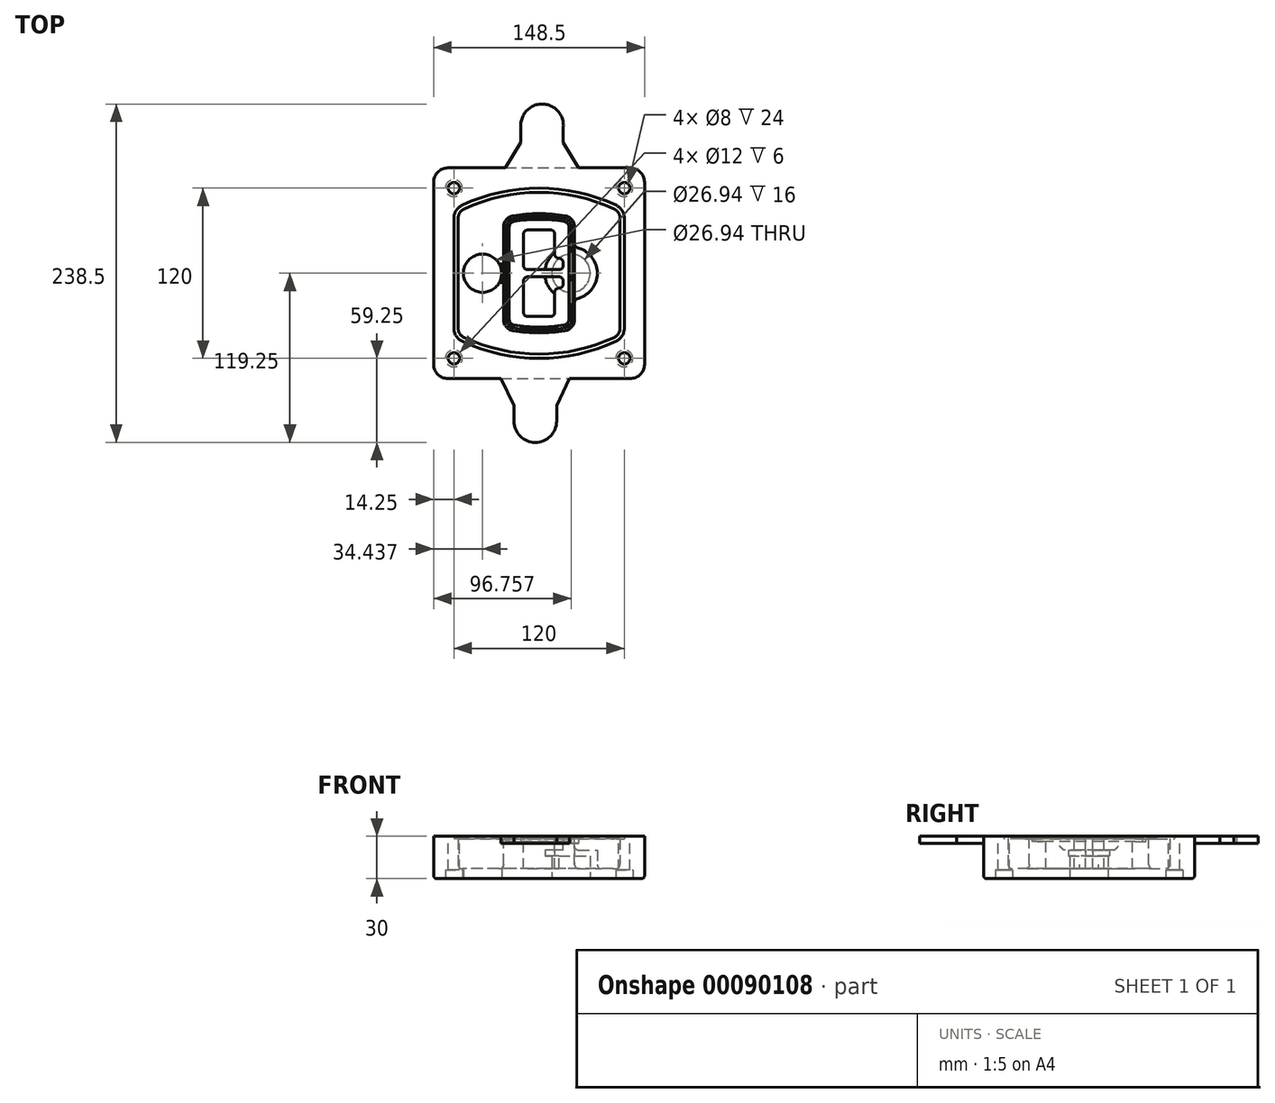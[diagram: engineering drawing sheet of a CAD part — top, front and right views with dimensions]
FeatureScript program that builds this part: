
annotation { "Feature Type Name" : "Feature", "Feature Type Description" : "" }
export const myFeature = defineFeature(function(context is Context, id is Id, definition is map)
    precondition{}
    {
        {
            var Q0;
            Q0=qCreatedBy(makeId("Top.planeOp"),FACE);
            var sketch = newSketch(context, id + "F0", { "sketchPlane" : qUnion([Q0])});
            skPoint(sketch, "E0.rect.middle", {"position": v(0, 0) * mm});
            skLineSegment(sketch, "E1.bottom", {"start": v(-64.25, -74.25) * mm, "end": v(64.25, -74.25) * mm});
            skLineSegment(sketch, "E1.top", {"start": v(-64.25, 74.25) * mm, "end": v(64.25, 74.25) * mm});
            skLineSegment(sketch, "E1.left", {"start": v(-74.25, -64.25) * mm, "end": v(-74.25, 64.25) * mm});
            skLineSegment(sketch, "E1.right", {"start": v(74.25, -64.25) * mm, "end": v(74.25, 64.25) * mm});
            skLineSegment(sketch, "E2", {"start": v(-74.25, 74.25) * mm, "end": v(74.25, -74.25) * mm, "construction": true});
            skLineSegment(sketch, "E3", {"start": v(74.25, 74.25) * mm, "end": v(-74.25, -74.25) * mm, "construction": true});
            skCircle(sketch, "E4", {"center": v(-60, 60) * mm, "radius": 4 * mm});
            skCircle(sketch, "E5", {"center": v(60, 60) * mm, "radius": 4 * mm});
            skCircle(sketch, "E6", {"center": v(60, -60) * mm, "radius": 4 * mm});
            skCircle(sketch, "E7", {"center": v(-60, -60) * mm, "radius": 4 * mm});
            skLineSegment(sketch, "E8", {"start": v(-60, 60) * mm, "end": v(60, 60) * mm, "construction": true});
            skLineSegment(sketch, "E9", {"start": v(60, 60) * mm, "end": v(60, -60) * mm, "construction": true});
            skLineSegment(sketch, "E10", {"start": v(60, -60) * mm, "end": v(-60, -60) * mm, "construction": true});
            skLineSegment(sketch, "E11", {"start": v(-60, -60) * mm, "end": v(-60, 60) * mm, "construction": true});
            skLineSegment(sketch, "E12", {"start": v(-60, 38.83) * mm, "end": v(-60, -38.83) * mm});
            skLineSegment(sketch, "E13", {"start": v(60, 38.83) * mm, "end": v(60, -38.83) * mm});
            skArc(sketch, "E14", {"start": v(54.26, 47.88) * mm, "mid": v(0, 60) * mm, "end": v(-54.26, 47.88) * mm});
            skArc(sketch, "E15", {"start": v(-54.26, -47.88) * mm, "mid": v(0, -60) * mm, "end": v(54.26, -47.88) * mm});
            skLineSegment(sketch, "E16", {"start": v(-60, 0) * mm, "end": v(60, 0) * mm, "construction": true});
            skPoint(sketch, "E17.visualSharp", {"position": v(-60, -45) * mm});
            skArc(sketch, "E17.filletArc", {"start": v(-60, -38.83) * mm, "mid": v(-58.44, -44.2) * mm, "end": v(-54.26, -47.88) * mm});
            skPoint(sketch, "E18.visualSharp", {"position": v(-60, 45) * mm});
            skArc(sketch, "E18.filletArc", {"start": v(-54.26, 47.88) * mm, "mid": v(-58.44, 44.2) * mm, "end": v(-60, 38.83) * mm});
            skPoint(sketch, "E19.visualSharp", {"position": v(60, 45) * mm});
            skArc(sketch, "E19.filletArc", {"start": v(60, 38.83) * mm, "mid": v(58.44, 44.2) * mm, "end": v(54.26, 47.88) * mm});
            skPoint(sketch, "E20.visualSharp", {"position": v(60, -45) * mm});
            skArc(sketch, "E20.filletArc", {"start": v(54.26, -47.88) * mm, "mid": v(58.44, -44.2) * mm, "end": v(60, -38.83) * mm});
            skPoint(sketch, "E21.visualSharp", {"position": v(-74.25, 74.25) * mm});
            skArc(sketch, "E21.filletArc", {"start": v(-64.25, 74.25) * mm, "mid": v(-71.32, 71.32) * mm, "end": v(-74.25, 64.25) * mm});
            skPoint(sketch, "E22.visualSharp", {"position": v(74.25, 74.25) * mm});
            skArc(sketch, "E22.filletArc", {"start": v(74.25, 64.25) * mm, "mid": v(71.32, 71.32) * mm, "end": v(64.25, 74.25) * mm});
            skPoint(sketch, "E23.visualSharp", {"position": v(74.25, -74.25) * mm});
            skArc(sketch, "E23.filletArc", {"start": v(64.25, -74.25) * mm, "mid": v(71.32, -71.32) * mm, "end": v(74.25, -64.25) * mm});
            skPoint(sketch, "E24.visualSharp", {"position": v(-74.25, -74.25) * mm});
            skArc(sketch, "E24.filletArc", {"start": v(-74.25, -64.25) * mm, "mid": v(-71.32, -71.32) * mm, "end": v(-64.25, -74.25) * mm});
            skArc(sketch, "E25.0", {"start": v(57, 38.83) * mm, "mid": v(55.9, 42.58) * mm, "end": v(52.98, 45.17) * mm});
            skLineSegment(sketch, "E25.1", {"start": v(57, 38.83) * mm, "end": v(57, -38.83) * mm});
            skArc(sketch, "E25.2", {"start": v(52.98, -45.17) * mm, "mid": v(55.9, -42.58) * mm, "end": v(57, -38.83) * mm});
            skArc(sketch, "E25.3", {"start": v(-52.98, -45.17) * mm, "mid": v(0, -57) * mm, "end": v(52.98, -45.17) * mm});
            skArc(sketch, "E25.4", {"start": v(-57, -38.83) * mm, "mid": v(-55.9, -42.58) * mm, "end": v(-52.98, -45.17) * mm});
            skArc(sketch, "E25.5", {"start": v(52.98, 45.17) * mm, "mid": v(0, 57) * mm, "end": v(-52.98, 45.17) * mm});
            skLineSegment(sketch, "E25.6", {"start": v(-57, 38.83) * mm, "end": v(-57, -38.83) * mm});
            skArc(sketch, "E25.7", {"start": v(-52.98, 45.17) * mm, "mid": v(-55.9, 42.58) * mm, "end": v(-57, 38.83) * mm});
            skArc(sketch, "E26.0", {"start": v(-55.96, 51.5) * mm, "mid": v(-61.82, 46.33) * mm, "end": v(-64, 38.83) * mm});
            skArc(sketch, "E26.1", {"start": v(55.96, 51.5) * mm, "mid": v(0, 64) * mm, "end": v(-55.96, 51.5) * mm});
            skArc(sketch, "E26.2", {"start": v(64, 38.83) * mm, "mid": v(61.82, 46.33) * mm, "end": v(55.96, 51.5) * mm});
            skLineSegment(sketch, "E26.3", {"start": v(64, 38.83) * mm, "end": v(64, -38.83) * mm});
            skArc(sketch, "E26.4", {"start": v(55.96, -51.5) * mm, "mid": v(61.82, -46.33) * mm, "end": v(64, -38.83) * mm});
            skLineSegment(sketch, "E26.5", {"start": v(-64, 38.83) * mm, "end": v(-64, -38.83) * mm});
            skArc(sketch, "E26.6", {"start": v(-55.96, -51.5) * mm, "mid": v(0, -64) * mm, "end": v(55.96, -51.5) * mm});
            skArc(sketch, "E26.7", {"start": v(-64, -38.83) * mm, "mid": v(-61.82, -46.33) * mm, "end": v(-55.96, -51.5) * mm});
            skSolve(sketch);
        }
        {
            var Q0;
            Q0=makeQuery(id+"F0.imprint","IMPRINT",FACE,{"disambiguationData":[TD([[makeQuery(id+"F0.imprint","IMPRINT",EDGE,{"derivedFrom":sQuery(id+"F0.wireOp",EDGE,"E1.bottom")}),1.0]])]});
            var Q1;
            Q1=makeQuery(id+"F0.imprint","IMPRINT",FACE,{"disambiguationData":[TD([[makeQuery(id+"F0.imprint","IMPRINT",EDGE,{"derivedFrom":sQuery(id+"F0.wireOp",EDGE,"E12")}),1.0]])]});
            var Q2;
            Q2=makeQuery(id+"F0.imprint","IMPRINT",FACE,{"disambiguationData":[TD([[makeQuery(id+"F0.imprint","IMPRINT",EDGE,{"derivedFrom":sQuery(id+"F0.wireOp",EDGE,"E25.0")}),1.0]])]});
            var Q3;
            Q3=makeQuery(id+"F0.imprint","IMPRINT",FACE,{"disambiguationData":[TD([[makeQuery(id+"F0.imprint","IMPRINT",EDGE,{"derivedFrom":sQuery(id+"F0.wireOp",EDGE,"E12")}),-1.0]])]});
            extrude(context, id + "F1", {"entities" : qUnion([Q0, Q1, Q2, Q3]), "oppositeDirection" : true, "depth" : 25 * mm});
        }
        {
            var Q0;
            Q0=makeQuery(id+"F0.imprint","IMPRINT",FACE,{"disambiguationData":[TD([[makeQuery(id+"F0.imprint","IMPRINT",EDGE,{"derivedFrom":sQuery(id+"F0.wireOp",EDGE,"E12")}),1.0]])]});
            extrude(context, id + "F2", {"entities" : qUnion([Q0]), "operationType" : NewBodyOperationType.ADD, "depth" : 3 * mm});
        }
        {
            var Q0;
            Q0=makeQuery(id+"F0.imprint","IMPRINT",FACE,{"disambiguationData":[TD([[makeQuery(id+"F0.imprint","IMPRINT",EDGE,{"derivedFrom":sQuery(id+"F0.wireOp",EDGE,"E25.0")}),1.0]])]});
            extrude(context, id + "F3", {"entities" : qUnion([Q0]), "operationType" : NewBodyOperationType.REMOVE, "oppositeDirection" : true, "depth" : 18 * mm});
        }
        {
            var Q0;
            Q0=makeQuery(id+"F2.opExtrude","CAP_FACE",FACE,{"disambiguationData":[OSD([sQuery(id+"F0.wireOp",EDGE,"E12"),sQuery(id+"F0.wireOp",EDGE,"E13"),sQuery(id+"F0.wireOp",EDGE,"E14"),sQuery(id+"F0.wireOp",EDGE,"E15"),sQuery(id+"F0.wireOp",EDGE,"E17.filletArc"),sQuery(id+"F0.wireOp",EDGE,"E18.filletArc"),sQuery(id+"F0.wireOp",EDGE,"E19.filletArc"),sQuery(id+"F0.wireOp",EDGE,"E20.filletArc"),sQuery(id+"F0.wireOp",EDGE,"E25.0"),sQuery(id+"F0.wireOp",EDGE,"E25.1"),sQuery(id+"F0.wireOp",EDGE,"E25.2"),sQuery(id+"F0.wireOp",EDGE,"E25.3"),sQuery(id+"F0.wireOp",EDGE,"E25.4"),sQuery(id+"F0.wireOp",EDGE,"E25.5"),sQuery(id+"F0.wireOp",EDGE,"E25.6"),sQuery(id+"F0.wireOp",EDGE,"E25.7")])],"isStart":false});
            var sketch = newSketch(context, id + "F4", { "sketchPlane" : qUnion([Q0])});
            skArc(sketch, "E27.0", {"start": v(-18.34, -40.45) * mm, "mid": v(0, -42) * mm, "end": v(18.34, -40.45) * mm});
            skArc(sketch, "E28.0", {"start": v(18.34, 40.45) * mm, "mid": v(0, 42) * mm, "end": v(-18.34, 40.45) * mm});
            skLineSegment(sketch, "E29", {"start": v(-25, 32.57) * mm, "end": v(-25, -32.57) * mm});
            skLineSegment(sketch, "E30", {"start": v(25, 32.57) * mm, "end": v(25, -32.57) * mm});
            skLineSegment(sketch, "E31", {"start": v(-25, 39.1) * mm, "end": v(25, 39.1) * mm, "construction": true});
            skLineSegment(sketch, "E32", {"start": v(-25, -39.1) * mm, "end": v(25, -39.1) * mm, "construction": true});
            skPoint(sketch, "E33.visualSharp", {"position": v(-25, 39.1) * mm});
            skArc(sketch, "E33.filletArc", {"start": v(-18.34, 40.45) * mm, "mid": v(-23.11, 37.73) * mm, "end": v(-25, 32.57) * mm});
            skPoint(sketch, "E34.visualSharp", {"position": v(25, 39.1) * mm});
            skArc(sketch, "E34.filletArc", {"start": v(25, 32.57) * mm, "mid": v(23.11, 37.73) * mm, "end": v(18.34, 40.45) * mm});
            skPoint(sketch, "E35.visualSharp", {"position": v(25, -39.1) * mm});
            skArc(sketch, "E35.filletArc", {"start": v(18.34, -40.45) * mm, "mid": v(23.11, -37.73) * mm, "end": v(25, -32.57) * mm});
            skPoint(sketch, "E36.visualSharp", {"position": v(-25, -39.1) * mm});
            skArc(sketch, "E36.filletArc", {"start": v(-25, -32.57) * mm, "mid": v(-23.11, -37.73) * mm, "end": v(-18.34, -40.45) * mm});
            skArc(sketch, "E37.0", {"start": v(52.98, 45.17) * mm, "mid": v(0, 57) * mm, "end": v(-52.98, 45.17) * mm});
            skArc(sketch, "E37.1", {"start": v(-52.98, 45.17) * mm, "mid": v(-55.9, 42.58) * mm, "end": v(-57, 38.83) * mm});
            skLineSegment(sketch, "E37.2", {"start": v(-57, 38.83) * mm, "end": v(-57, -38.83) * mm});
            skArc(sketch, "E37.3", {"start": v(-57, -38.83) * mm, "mid": v(-55.9, -42.58) * mm, "end": v(-52.98, -45.17) * mm});
            skArc(sketch, "E37.4", {"start": v(-52.98, -45.17) * mm, "mid": v(0, -57) * mm, "end": v(52.98, -45.17) * mm});
            skArc(sketch, "E37.5", {"start": v(52.98, -45.17) * mm, "mid": v(55.9, -42.58) * mm, "end": v(57, -38.83) * mm});
            skLineSegment(sketch, "E37.6", {"start": v(57, 38.83) * mm, "end": v(57, -38.83) * mm});
            skArc(sketch, "E37.7", {"start": v(57, 38.83) * mm, "mid": v(55.9, 42.58) * mm, "end": v(52.98, 45.17) * mm});
            skLineSegment(sketch, "E38.0", {"start": v(23, 32.57) * mm, "end": v(23, -32.57) * mm});
            skArc(sketch, "E38.1", {"start": v(18, -38.48) * mm, "mid": v(21.58, -36.44) * mm, "end": v(23, -32.57) * mm});
            skArc(sketch, "E38.2", {"start": v(-18, -38.48) * mm, "mid": v(0, -40) * mm, "end": v(18, -38.48) * mm});
            skArc(sketch, "E38.3", {"start": v(-23, -32.57) * mm, "mid": v(-21.58, -36.44) * mm, "end": v(-18, -38.48) * mm});
            skLineSegment(sketch, "E38.4", {"start": v(-23, 32.57) * mm, "end": v(-23, -32.57) * mm});
            skArc(sketch, "E38.5", {"start": v(23, 32.57) * mm, "mid": v(21.58, 36.44) * mm, "end": v(18, 38.48) * mm});
            skArc(sketch, "E38.6", {"start": v(-18, 38.48) * mm, "mid": v(-21.58, 36.44) * mm, "end": v(-23, 32.57) * mm});
            skArc(sketch, "E38.7", {"start": v(18, 38.48) * mm, "mid": v(0, 40) * mm, "end": v(-18, 38.48) * mm});
            skArc(sketch, "E39.0", {"start": v(21, 32.57) * mm, "mid": v(20.06, 35.15) * mm, "end": v(17.67, 36.5) * mm});
            skLineSegment(sketch, "E39.1", {"start": v(21, 32.57) * mm, "end": v(21, -32.57) * mm});
            skArc(sketch, "E39.2", {"start": v(17.67, -36.5) * mm, "mid": v(20.06, -35.15) * mm, "end": v(21, -32.57) * mm});
            skArc(sketch, "E39.3", {"start": v(-17.67, -36.5) * mm, "mid": v(0, -38) * mm, "end": v(17.67, -36.5) * mm});
            skArc(sketch, "E39.4", {"start": v(-21, -32.57) * mm, "mid": v(-20.06, -35.15) * mm, "end": v(-17.67, -36.5) * mm});
            skArc(sketch, "E39.5", {"start": v(17.67, 36.5) * mm, "mid": v(0, 38) * mm, "end": v(-17.67, 36.5) * mm});
            skLineSegment(sketch, "E39.6", {"start": v(-21, 32.57) * mm, "end": v(-21, -32.57) * mm});
            skArc(sketch, "E39.7", {"start": v(-17.67, 36.5) * mm, "mid": v(-20.06, 35.15) * mm, "end": v(-21, 32.57) * mm});
            skLineSegment(sketch, "E40", {"start": v(-25, 0) * mm, "end": v(25, 0) * mm, "construction": true});
            skLineSegment(sketch, "E41", {"start": v(-11, 5.5) * mm, "end": v(-11, 27.5) * mm});
            skLineSegment(sketch, "E42", {"start": v(-8, 30.5) * mm, "end": v(8, 30.5) * mm});
            skLineSegment(sketch, "E43", {"start": v(11, 27.5) * mm, "end": v(11, 13.5) * mm});
            skLineSegment(sketch, "E44", {"start": v(14, 10.5) * mm, "end": v(14, 10.5) * mm});
            skLineSegment(sketch, "E45", {"start": v(17, 7.5) * mm, "end": v(17, 5.5) * mm});
            skLineSegment(sketch, "E46", {"start": v(14, 2.5) * mm, "end": v(-8, 2.5) * mm});
            skPoint(sketch, "E47.visualSharp", {"position": v(-11, 30.5) * mm});
            skArc(sketch, "E47.filletArc", {"start": v(-8, 30.5) * mm, "mid": v(-10.12, 29.62) * mm, "end": v(-11, 27.5) * mm});
            skPoint(sketch, "E48.visualSharp", {"position": v(11, 30.5) * mm});
            skArc(sketch, "E48.filletArc", {"start": v(11, 27.5) * mm, "mid": v(10.12, 29.62) * mm, "end": v(8, 30.5) * mm});
            skPoint(sketch, "E49.visualSharp", {"position": v(11, 10.5) * mm});
            skArc(sketch, "E49.filletArc", {"start": v(11, 13.5) * mm, "mid": v(11.88, 11.38) * mm, "end": v(14, 10.5) * mm});
            skPoint(sketch, "E50.visualSharp", {"position": v(17, 10.5) * mm});
            skArc(sketch, "E50.filletArc", {"start": v(17, 7.5) * mm, "mid": v(16.12, 9.62) * mm, "end": v(14, 10.5) * mm});
            skPoint(sketch, "E51.visualSharp", {"position": v(17, 2.5) * mm});
            skArc(sketch, "E51.filletArc", {"start": v(14, 2.5) * mm, "mid": v(16.12, 3.38) * mm, "end": v(17, 5.5) * mm});
            skPoint(sketch, "E52.visualSharp", {"position": v(-11, 2.5) * mm});
            skArc(sketch, "E52.filletArc", {"start": v(-11, 5.5) * mm, "mid": v(-10.12, 3.38) * mm, "end": v(-8, 2.5) * mm});
            skLineSegment(sketch, "E53.0.MirrorCS", {"start": v(14, -2.5) * mm, "end": v(-8, -2.5) * mm});
            skArc(sketch, "E54.0.MirrorCS", {"start": v(-11, -5.5) * mm, "mid": v(-10.12, -3.38) * mm, "end": v(-8, -2.5) * mm});
            skLineSegment(sketch, "E55.0.MirrorCS", {"start": v(-11, -5.5) * mm, "end": v(-11, -27.5) * mm});
            skArc(sketch, "E56.0.MirrorCS", {"start": v(-8, -30.5) * mm, "mid": v(-10.12, -29.62) * mm, "end": v(-11, -27.5) * mm});
            skLineSegment(sketch, "E57.0.MirrorCS", {"start": v(-8, -30.5) * mm, "end": v(8, -30.5) * mm});
            skArc(sketch, "E58.0.MirrorCS", {"start": v(11, -27.5) * mm, "mid": v(10.12, -29.62) * mm, "end": v(8, -30.5) * mm});
            skLineSegment(sketch, "E59.0.MirrorCS", {"start": v(11, -27.5) * mm, "end": v(11, -13.5) * mm});
            skArc(sketch, "E60.0.MirrorCS", {"start": v(11, -13.5) * mm, "mid": v(11.88, -11.38) * mm, "end": v(14, -10.5) * mm});
            skArc(sketch, "E61.0.MirrorCS", {"start": v(17, -7.5) * mm, "mid": v(16.12, -9.62) * mm, "end": v(14, -10.5) * mm});
            skLineSegment(sketch, "E62.0.MirrorCS", {"start": v(17, -7.5) * mm, "end": v(17, -5.5) * mm});
            skArc(sketch, "E63.0.MirrorCS", {"start": v(14, -2.5) * mm, "mid": v(16.12, -3.38) * mm, "end": v(17, -5.5) * mm});
            skSolve(sketch);
        }
        {
            var Q0;
            Q0=makeQuery(id+"F4.imprint","IMPRINT",FACE,{"disambiguationData":[TD([[makeQuery(id+"F4.imprint","IMPRINT",EDGE,{"derivedFrom":sQuery(id+"F4.wireOp",EDGE,"E27.0")}),1.0]])]});
            var Q1;
            Q1=makeQuery(id+"F4.imprint","IMPRINT",FACE,{"disambiguationData":[TD([[makeQuery(id+"F4.imprint","IMPRINT",EDGE,{"derivedFrom":sQuery(id+"F4.wireOp",EDGE,"E38.0")}),-1.0]])]});
            var Q2;
            Q2=makeQuery(id+"F4.imprint","IMPRINT",FACE,{"disambiguationData":[TD([[makeQuery(id+"F4.imprint","IMPRINT",EDGE,{"derivedFrom":sQuery(id+"F4.wireOp",EDGE,"E39.0")}),1.0]])]});
            extrude(context, id + "F5", {"entities" : qUnion([Q0, Q1, Q2]), "operationType" : NewBodyOperationType.ADD, "endBound" : BoundingType.UP_TO_NEXT, "oppositeDirection" : true, "depth" : 25 * mm});
        }
        {
            var Q0;
            Q0=makeQuery(id+"F4.imprint","IMPRINT",FACE,{"disambiguationData":[TD([[makeQuery(id+"F4.imprint","IMPRINT",EDGE,{"derivedFrom":sQuery(id+"F4.wireOp",EDGE,"E38.0")}),-1.0]])]});
            extrude(context, id + "F6", {"entities" : qUnion([Q0]), "operationType" : NewBodyOperationType.REMOVE, "oppositeDirection" : true, "depth" : 2 * mm});
        }
        {
            var Q0;
            Q0=makeQuery(id+"F1.opExtrude","CAP_FACE",FACE,{"disambiguationData":[OSD([sQuery(id+"F0.wireOp",EDGE,"E1.bottom"),sQuery(id+"F0.wireOp",EDGE,"E1.top"),sQuery(id+"F0.wireOp",EDGE,"E1.left"),sQuery(id+"F0.wireOp",EDGE,"E1.right"),sQuery(id+"F0.wireOp",EDGE,"E4"),sQuery(id+"F0.wireOp",EDGE,"E5"),sQuery(id+"F0.wireOp",EDGE,"E6"),sQuery(id+"F0.wireOp",EDGE,"E7"),sQuery(id+"F0.wireOp",EDGE,"E21.filletArc"),sQuery(id+"F0.wireOp",EDGE,"E22.filletArc"),sQuery(id+"F0.wireOp",EDGE,"E23.filletArc"),sQuery(id+"F0.wireOp",EDGE,"E24.filletArc")])],"isStart":false});
            var sketch = newSketch(context, id + "F7", { "sketchPlane" : qUnion([Q0])});
            skCircle(sketch, "E64", {"center": v(22.5, 0) * mm, "radius": 13.47 * mm});
            skCircle(sketch, "E65", {"center": v(-39.81, 0) * mm, "radius": 13.47 * mm});
            skLineSegment(sketch, "E66", {"start": v(74.25, 0) * mm, "end": v(-74.25, 0) * mm});
            skCircle(sketch, "E67", {"center": v(22.5, 0) * mm, "radius": 18.47 * mm});
            skCircle(sketch, "E68", {"center": v(60, -60) * mm, "radius": 6 * mm});
            skCircle(sketch, "E69", {"center": v(-60, -60) * mm, "radius": 6 * mm});
            skCircle(sketch, "E70", {"center": v(-60, 60) * mm, "radius": 6 * mm});
            skCircle(sketch, "E71", {"center": v(60, 60) * mm, "radius": 6 * mm});
            skSolve(sketch);
        }
        {
            var Q0;
            {var subQ1=sQuery(id+"F7.wireOp",EDGE,"E66");var subQ4=sQuery(id+"F7.wireOp",EDGE,"E64");var subQ6=makeQuery(id+"F7.imprint","INTERSECT",VERTEX,{"disambiguationData":[OD(0.0)],"derivedFrom":[subQ4,subQ1]});Q0=makeQuery(id+"F7.imprint","IMPRINT",FACE,{"disambiguationData":[TD([[makeQuery(id+"F7.imprint","IMPRINT",EDGE,{"disambiguationData":[TD([[subQ6,-1.0]])],"derivedFrom":subQ4}),-1.0]])]});}
            var Q1;
            {var subQ0=sQuery(id+"F7.wireOp",EDGE,"E66");var subQ1=sQuery(id+"F7.wireOp",EDGE,"E64");var subQ3=makeQuery(id+"F7.imprint","INTERSECT",VERTEX,{"disambiguationData":[OD(0.0)],"derivedFrom":[subQ1,subQ0]});Q1=makeQuery(id+"F7.imprint","IMPRINT",FACE,{"disambiguationData":[TD([[makeQuery(id+"F7.imprint","IMPRINT",EDGE,{"disambiguationData":[TD([[subQ3,-1.0]])],"derivedFrom":subQ1}),1.0]])]});}
            var Q2;
            {var subQ0=sQuery(id+"F7.wireOp",EDGE,"E66");var subQ1=sQuery(id+"F7.wireOp",EDGE,"E64");var subQ3=makeQuery(id+"F7.imprint","INTERSECT",VERTEX,{"disambiguationData":[OD(0.0)],"derivedFrom":[subQ1,subQ0]});Q2=makeQuery(id+"F7.imprint","IMPRINT",FACE,{"disambiguationData":[TD([[makeQuery(id+"F7.imprint","IMPRINT",EDGE,{"disambiguationData":[TD([[subQ3,1.0]])],"derivedFrom":subQ1}),1.0]])]});}
            var Q3;
            {var subQ1=sQuery(id+"F7.wireOp",EDGE,"E66");var subQ4=sQuery(id+"F7.wireOp",EDGE,"E64");var subQ6=makeQuery(id+"F7.imprint","INTERSECT",VERTEX,{"disambiguationData":[OD(0.0)],"derivedFrom":[subQ4,subQ1]});Q3=makeQuery(id+"F7.imprint","IMPRINT",FACE,{"disambiguationData":[TD([[makeQuery(id+"F7.imprint","IMPRINT",EDGE,{"disambiguationData":[TD([[subQ6,1.0]])],"derivedFrom":subQ4}),-1.0]])]});}
            extrude(context, id + "F8", {"entities" : qUnion([Q0, Q1, Q2, Q3]), "operationType" : NewBodyOperationType.ADD, "oppositeDirection" : true, "depth" : 20 * mm});
        }
        {
            var Q0;
            {var subQ0=sQuery(id+"F7.wireOp",EDGE,"E66");var subQ1=sQuery(id+"F7.wireOp",EDGE,"E64");var subQ3=makeQuery(id+"F7.imprint","INTERSECT",VERTEX,{"disambiguationData":[OD(0.0)],"derivedFrom":[subQ1,subQ0]});Q0=makeQuery(id+"F7.imprint","IMPRINT",FACE,{"disambiguationData":[TD([[makeQuery(id+"F7.imprint","IMPRINT",EDGE,{"disambiguationData":[TD([[subQ3,-1.0]])],"derivedFrom":subQ1}),1.0]])]});}
            var Q1;
            {var subQ0=sQuery(id+"F7.wireOp",EDGE,"E66");var subQ1=sQuery(id+"F7.wireOp",EDGE,"E64");var subQ3=makeQuery(id+"F7.imprint","INTERSECT",VERTEX,{"disambiguationData":[OD(0.0)],"derivedFrom":[subQ1,subQ0]});Q1=makeQuery(id+"F7.imprint","IMPRINT",FACE,{"disambiguationData":[TD([[makeQuery(id+"F7.imprint","IMPRINT",EDGE,{"disambiguationData":[TD([[subQ3,1.0]])],"derivedFrom":subQ1}),1.0]])]});}
            extrude(context, id + "F9", {"entities" : qUnion([Q0, Q1]), "operationType" : NewBodyOperationType.REMOVE, "oppositeDirection" : true, "depth" : 16 * mm});
        }
        {
            var Q0;
            {var subQ0=sQuery(id+"F7.wireOp",EDGE,"E66");var subQ1=sQuery(id+"F7.wireOp",EDGE,"E65");var subQ3=makeQuery(id+"F7.imprint","INTERSECT",VERTEX,{"disambiguationData":[OD(0.0)],"derivedFrom":[subQ1,subQ0]});Q0=makeQuery(id+"F7.imprint","IMPRINT",FACE,{"disambiguationData":[TD([[makeQuery(id+"F7.imprint","IMPRINT",EDGE,{"disambiguationData":[TD([[subQ3,-1.0]])],"derivedFrom":subQ1}),1.0]])]});}
            var Q1;
            {var subQ0=sQuery(id+"F7.wireOp",EDGE,"E66");var subQ1=sQuery(id+"F7.wireOp",EDGE,"E65");var subQ3=makeQuery(id+"F7.imprint","INTERSECT",VERTEX,{"disambiguationData":[OD(0.0)],"derivedFrom":[subQ1,subQ0]});Q1=makeQuery(id+"F7.imprint","IMPRINT",FACE,{"disambiguationData":[TD([[makeQuery(id+"F7.imprint","IMPRINT",EDGE,{"disambiguationData":[TD([[subQ3,1.0]])],"derivedFrom":subQ1}),1.0]])]});}
            extrude(context, id + "F10", {"entities" : qUnion([Q0, Q1]), "operationType" : NewBodyOperationType.REMOVE, "oppositeDirection" : true, "depth" : 25 * mm});
        }
        {
            var Q0;
            Q0=makeQuery(id+"F7.imprint","IMPRINT",FACE,{"disambiguationData":[TD([[makeQuery(id+"F7.imprint","IMPRINT",EDGE,{"derivedFrom":sQuery(id+"F7.wireOp",EDGE,"E68")}),1.0]])]});
            var Q1;
            Q1=makeQuery(id+"F7.imprint","IMPRINT",FACE,{"disambiguationData":[TD([[makeQuery(id+"F7.imprint","IMPRINT",EDGE,{"derivedFrom":makeQuery(id+"F1.opExtrude","CAP_EDGE",EDGE,{"disambiguationData":[OSD([sQuery(id+"F0.wireOp",EDGE,"E5")])],"isStart":false})}),-1.0]])]});
            var Q2;
            Q2=makeQuery(id+"F7.imprint","IMPRINT",FACE,{"disambiguationData":[TD([[makeQuery(id+"F7.imprint","IMPRINT",EDGE,{"derivedFrom":sQuery(id+"F7.wireOp",EDGE,"E69")}),1.0]])]});
            var Q3;
            Q3=makeQuery(id+"F7.imprint","IMPRINT",FACE,{"disambiguationData":[TD([[makeQuery(id+"F7.imprint","IMPRINT",EDGE,{"derivedFrom":makeQuery(id+"F1.opExtrude","CAP_EDGE",EDGE,{"disambiguationData":[OSD([sQuery(id+"F0.wireOp",EDGE,"E4")])],"isStart":false})}),-1.0]])]});
            var Q4;
            Q4=makeQuery(id+"F7.imprint","IMPRINT",FACE,{"disambiguationData":[TD([[makeQuery(id+"F7.imprint","IMPRINT",EDGE,{"derivedFrom":sQuery(id+"F7.wireOp",EDGE,"E70")}),1.0]])]});
            var Q5;
            Q5=makeQuery(id+"F7.imprint","IMPRINT",FACE,{"disambiguationData":[TD([[makeQuery(id+"F7.imprint","IMPRINT",EDGE,{"derivedFrom":makeQuery(id+"F1.opExtrude","CAP_EDGE",EDGE,{"disambiguationData":[OSD([sQuery(id+"F0.wireOp",EDGE,"E7")])],"isStart":false})}),-1.0]])]});
            var Q6;
            Q6=makeQuery(id+"F7.imprint","IMPRINT",FACE,{"disambiguationData":[TD([[makeQuery(id+"F7.imprint","IMPRINT",EDGE,{"derivedFrom":sQuery(id+"F7.wireOp",EDGE,"E71")}),1.0]])]});
            var Q7;
            Q7=makeQuery(id+"F7.imprint","IMPRINT",FACE,{"disambiguationData":[TD([[makeQuery(id+"F7.imprint","IMPRINT",EDGE,{"derivedFrom":makeQuery(id+"F1.opExtrude","CAP_EDGE",EDGE,{"disambiguationData":[OSD([sQuery(id+"F0.wireOp",EDGE,"E6")])],"isStart":false})}),-1.0]])]});
            extrude(context, id + "F11", {"entities" : qUnion([Q0, Q1, Q2, Q3, Q4, Q5, Q6, Q7]), "operationType" : NewBodyOperationType.REMOVE, "oppositeDirection" : true, "depth" : 6 * mm});
        }
        {
            var Q0;
            Q0=makeQuery(id+"F9.boolean.opBoolean","COPY",FACE,{"derivedFrom":makeQuery(id+"F9.opExtrude","CAP_FACE",FACE,{"disambiguationData":[OSD([sQuery(id+"F7.wireOp",EDGE,"E64")])],"isStart":false})});
            var sketch = newSketch(context, id + "F12", { "sketchPlane" : qUnion([Q0])});
            skArc(sketch, "E72.0", {"start": v(11, 14.45) * mm, "mid": v(6.45, 9.13) * mm, "end": v(4.2, 2.5) * mm});
            skArc(sketch, "E72.1", {"start": v(4.2, -2.5) * mm, "mid": v(6.45, -9.13) * mm, "end": v(11, -14.45) * mm});
            skLineSegment(sketch, "E73", {"start": v(4.2, -2.5) * mm, "end": v(14, -2.5) * mm});
            skLineSegment(sketch, "E74.0", {"start": v(14, 2.5) * mm, "end": v(4.2, 2.5) * mm});
            skArc(sketch, "E74.1", {"start": v(14, 2.5) * mm, "mid": v(16.12, 3.38) * mm, "end": v(17, 5.5) * mm});
            skLineSegment(sketch, "E74.2", {"start": v(17, 7.5) * mm, "end": v(17, 5.5) * mm});
            skArc(sketch, "E74.3", {"start": v(17, 7.5) * mm, "mid": v(16.12, 9.62) * mm, "end": v(14, 10.5) * mm});
            skArc(sketch, "E74.4", {"start": v(11, 13.5) * mm, "mid": v(11.88, 11.38) * mm, "end": v(14, 10.5) * mm});
            skLineSegment(sketch, "E74.5", {"start": v(11, 14.45) * mm, "end": v(11, 13.5) * mm});
            skLineSegment(sketch, "E74.7", {"start": v(14, -2.5) * mm, "end": v(4.2, -2.5) * mm});
            skArc(sketch, "E74.8", {"start": v(14, -2.5) * mm, "mid": v(16.12, -3.38) * mm, "end": v(17, -5.5) * mm});
            skLineSegment(sketch, "E74.9", {"start": v(17, -7.5) * mm, "end": v(17, -5.5) * mm});
            skArc(sketch, "E74.10", {"start": v(17, -7.5) * mm, "mid": v(16.12, -9.62) * mm, "end": v(14, -10.5) * mm});
            skArc(sketch, "E74.11", {"start": v(11, -13.5) * mm, "mid": v(11.88, -11.38) * mm, "end": v(14, -10.5) * mm});
            skLineSegment(sketch, "E74.12", {"start": v(11, -14.45) * mm, "end": v(11, -13.5) * mm});
            skPoint(sketch, "E75.orphan", {"position": v(11, -27.5) * mm});
            skPoint(sketch, "E76.orphan", {"position": v(-8, -2.5) * mm});
            skPoint(sketch, "E77.orphan", {"position": v(-8, 2.5) * mm});
            skPoint(sketch, "E78.orphan", {"position": v(11, 27.5) * mm});
            skSolve(sketch);
        }
        {
            var Q0;
            {var subQ7=sQuery(id+"F12.wireOp",EDGE,"E72.0");var subQ14=sQuery(id+"F12.wireOp",EDGE,"E72.1");var subQ16=sQuery(id+"F12.wireOp",EDGE,"E74.1");var subQ18=sQuery(id+"F12.wireOp",EDGE,"E74.8");Q0=qUnion([makeQuery(id+"F12.imprint","IMPRINT",FACE,{"disambiguationData":[TD([[makeQuery(id+"F12.imprint","IMPRINT",EDGE,{"derivedFrom":subQ7}),1.0]])]}),makeQuery(id+"F12.imprint","IMPRINT",FACE,{"disambiguationData":[TD([[makeQuery(id+"F12.imprint","IMPRINT",EDGE,{"derivedFrom":subQ14}),1.0]])]}),makeQuery(id+"F12.imprint","IMPRINT",FACE,{"disambiguationData":[TD([[makeQuery(id+"F12.imprint","IMPRINT",EDGE,{"derivedFrom":subQ16}),1.0]])]}),makeQuery(id+"F12.imprint","IMPRINT",FACE,{"disambiguationData":[TD([[makeQuery(id+"F12.imprint","IMPRINT",EDGE,{"derivedFrom":subQ18}),-1.0]])]})]);}
            var Q1;
            Q1=makeQuery(id+"F5.boolean.opBoolean","SPLIT",FACE,{"disambiguationData":[TD([makeQuery(id+"F5.opExtrude","SWEPT_FACE",FACE,{"disambiguationData":[OSD([sQuery(id+"F4.wireOp",EDGE,"E41")])]})])],"derivedFrom":makeQuery(id+"F3.boolean.opBoolean","COPY",FACE,{"derivedFrom":makeQuery(id+"F3.opExtrude","CAP_FACE",FACE,{"disambiguationData":[OSD([sQuery(id+"F0.wireOp",EDGE,"E25.0"),sQuery(id+"F0.wireOp",EDGE,"E25.1"),sQuery(id+"F0.wireOp",EDGE,"E25.2"),sQuery(id+"F0.wireOp",EDGE,"E25.3"),sQuery(id+"F0.wireOp",EDGE,"E25.4"),sQuery(id+"F0.wireOp",EDGE,"E25.5"),sQuery(id+"F0.wireOp",EDGE,"E25.6"),sQuery(id+"F0.wireOp",EDGE,"E25.7")])],"isStart":false})})});
            extrude(context, id + "F13", {"entities" : qUnion([Q0]), "operationType" : NewBodyOperationType.REMOVE, "endBound" : BoundingType.UP_TO_SURFACE, "endBoundEntityFace" : qUnion([Q1]), "depth" : 25 * mm});
        }
        {
            var Q0;
            Q0=makeQuery(id+"F3.boolean.opBoolean","COPY",EDGE,{"derivedFrom":makeQuery(id+"F3.opExtrude","CAP_EDGE",EDGE,{"disambiguationData":[OSD([sQuery(id+"F0.wireOp",EDGE,"E25.6")])],"isStart":false})});
            var Q1;
            Q1=makeQuery(id+"F8.boolean.opBoolean","INTERSECT",EDGE,{"derivedFrom":[makeQuery(id+"F5.opExtrude","SWEPT_FACE",FACE,{"disambiguationData":[OSD([sQuery(id+"F4.wireOp",EDGE,"E30")])]}),makeQuery(id+"F8.opExtrude","CAP_FACE",FACE,{"disambiguationData":[OSD([sQuery(id+"F7.wireOp",EDGE,"E67")])],"isStart":false})]});
            var Q2;
            Q2=makeQuery(id+"F8.boolean.opBoolean","INTERSECT",EDGE,{"disambiguationData":[OD(1.0)],"derivedFrom":[makeQuery(id+"F5.opExtrude","SWEPT_FACE",FACE,{"disambiguationData":[OSD([sQuery(id+"F4.wireOp",EDGE,"E30")])]}),makeQuery(id+"F8.opExtrude","SWEPT_FACE",FACE,{"disambiguationData":[OSD([sQuery(id+"F7.wireOp",EDGE,"E67")])]})]});
            var Q3;
            {var subQ0=sQuery(id+"F4.wireOp",EDGE,"E30");Q3=makeQuery(id+"F8.boolean.opBoolean","SPLIT",EDGE,{"disambiguationData":[TD([makeQuery(id+"F5.opExtrude","SWEPT_FACE",FACE,{"disambiguationData":[OSD([sQuery(id+"F4.wireOp",EDGE,"E35.filletArc")])]})])],"derivedFrom":makeQuery(id+"F5.opExtrude","CAP_EDGE",EDGE,{"disambiguationData":[OSD([subQ0])],"isStart":false})});}
            var Q4;
            {var subQ0=sQuery(id+"F0.wireOp",EDGE,"E25.7");var subQ1=sQuery(id+"F0.wireOp",EDGE,"E25.1");var subQ2=sQuery(id+"F0.wireOp",EDGE,"E25.6");var subQ3=sQuery(id+"F0.wireOp",EDGE,"E25.5");var subQ4=sQuery(id+"F0.wireOp",EDGE,"E25.4");var subQ5=sQuery(id+"F0.wireOp",EDGE,"E25.0");var subQ6=sQuery(id+"F0.wireOp",EDGE,"E25.2");var subQ7=sQuery(id+"F0.wireOp",EDGE,"E25.3");Q4=makeQuery(id+"F8.boolean.opBoolean","INTERSECT",EDGE,{"derivedFrom":[makeQuery(id+"F5.boolean.opBoolean","SPLIT",FACE,{"disambiguationData":[TD([makeQuery(id+"F2.opExtrude","SWEPT_FACE",FACE,{"disambiguationData":[OSD([subQ5])]})])],"derivedFrom":makeQuery(id+"F3.boolean.opBoolean","COPY",FACE,{"derivedFrom":makeQuery(id+"F3.opExtrude","CAP_FACE",FACE,{"disambiguationData":[OSD([subQ5,subQ1,subQ6,subQ7,subQ4,subQ3,subQ2,subQ0])],"isStart":false})})}),makeQuery(id+"F8.opExtrude","SWEPT_FACE",FACE,{"disambiguationData":[OSD([sQuery(id+"F7.wireOp",EDGE,"E67")])]})]});}
            var Q5;
            Q5=makeQuery(id+"F8.boolean.opBoolean","INTERSECT",EDGE,{"disambiguationData":[OD(0.0)],"derivedFrom":[makeQuery(id+"F5.opExtrude","SWEPT_FACE",FACE,{"disambiguationData":[OSD([sQuery(id+"F4.wireOp",EDGE,"E30")])]}),makeQuery(id+"F8.opExtrude","SWEPT_FACE",FACE,{"disambiguationData":[OSD([sQuery(id+"F7.wireOp",EDGE,"E67")])]})]});
            fillet(context, id + "F14", {"entities" : qUnion([Q0, Q1, Q2, Q3, Q4, Q5]), "radius" : 3 * mm, "tangentPropagation" : true, "allowEdgeOverflow" : false});
        }
        {
            var Q0;
            Q0=makeQuery(id+"F1.opExtrude","CAP_EDGE",EDGE,{"disambiguationData":[OSD([sQuery(id+"F0.wireOp",EDGE,"E1.bottom")])],"isStart":false});
            fillet(context, id + "F15", {"entities" : qUnion([Q0]), "radius" : 2 * mm, "tangentPropagation" : true, "allowEdgeOverflow" : false});
        }
        {
            var Q0;
            {var subQ0=sQuery(id+"F0.wireOp",EDGE,"E22.filletArc");var subQ1=sQuery(id+"F0.wireOp",EDGE,"E7");var subQ2=sQuery(id+"F0.wireOp",EDGE,"E6");var subQ3=sQuery(id+"F0.wireOp",EDGE,"E5");var subQ4=sQuery(id+"F0.wireOp",EDGE,"E4");var subQ5=sQuery(id+"F0.wireOp",EDGE,"E1.bottom");var subQ6=sQuery(id+"F0.wireOp",EDGE,"E21.filletArc");var subQ7=sQuery(id+"F0.wireOp",EDGE,"E1.top");var subQ8=sQuery(id+"F0.wireOp",EDGE,"E1.left");var subQ9=sQuery(id+"F0.wireOp",EDGE,"E1.right");var subQ10=sQuery(id+"F0.wireOp",EDGE,"E23.filletArc");var subQ11=sQuery(id+"F0.wireOp",EDGE,"E24.filletArc");Q0=makeQuery(id+"F2.boolean.opBoolean","SPLIT",FACE,{"disambiguationData":[TD([makeQuery(id+"F1.opExtrude","SWEPT_FACE",FACE,{"disambiguationData":[OSD([subQ5])]})])],"derivedFrom":makeQuery(id+"F1.opExtrude","CAP_FACE",FACE,{"disambiguationData":[OSD([subQ5,subQ7,subQ8,subQ9,subQ4,subQ3,subQ2,subQ1,subQ6,subQ0,subQ10,subQ11])],"isStart":true})});}
            var sketch = newSketch(context, id + "F16", { "sketchPlane" : qUnion([Q0])});
            skLineSegment(sketch, "E79", {"start": v(-23.71, 74.25) * mm, "end": v(-12.9, 92.25) * mm});
            skLineSegment(sketch, "E80", {"start": v(27.75, 74.25) * mm, "end": v(16.93, 92.25) * mm});
            skLineSegment(sketch, "E81", {"start": v(-12.9, 92.25) * mm, "end": v(-12.9, 103.95) * mm});
            skLineSegment(sketch, "E82", {"start": v(16.93, 92.25) * mm, "end": v(16.93, 102.02) * mm});
            skArc(sketch, "E83", {"start": v(16.93, 102.02) * mm, "mid": v(3.07, 119.22) * mm, "end": v(-12.9, 103.95) * mm});
            skCircle(sketch, "E84", {"center": v(2.1, 104.25) * mm, "radius": 6 * mm});
            skLineSegment(sketch, "E85", {"start": v(-26.81, -74.25) * mm, "end": v(-17.65, -93.14) * mm});
            skLineSegment(sketch, "E86", {"start": v(-17.65, -93.14) * mm, "end": v(-17.65, -104.25) * mm});
            skLineSegment(sketch, "E87", {"start": v(21.3, -74.25) * mm, "end": v(12.35, -93.25) * mm});
            skLineSegment(sketch, "E88", {"start": v(12.35, -93.25) * mm, "end": v(12.35, -104.25) * mm});
            skArc(sketch, "E89", {"start": v(-17.65, -104.25) * mm, "mid": v(-2.65, -119.25) * mm, "end": v(12.35, -104.25) * mm});
            skCircle(sketch, "E90", {"center": v(-2.65, -104.25) * mm, "radius": 6 * mm});
            skLineSegment(sketch, "E91", {"start": v(2.1, 104.25) * mm, "end": v(0, 0) * mm, "construction": true});
            skLineSegment(sketch, "E92", {"start": v(0, 0) * mm, "end": v(-2.65, -104.25) * mm, "construction": true});
            skLineSegment(sketch, "E93", {"start": v(0, 0) * mm, "end": v(74.25, 0) * mm, "construction": true});
            skLineSegment(sketch, "E94", {"start": v(0, 0) * mm, "end": v(-74.25, 0) * mm, "construction": true});
            skSolve(sketch);
        }
        {
            var Q0;
            Q0 = qSketchRegion(id + "F16", true);
            var Q1;
            {var subQ0=sQuery(id+"F16.wireOp",EDGE,"E79");Q1=makeQuery(id+"F16.imprint","IMPRINT",FACE,{"disambiguationData":[TD([[makeQuery(id+"F16.imprint","IMPRINT",EDGE,{"derivedFrom":subQ0}),-1.0]])]});}
            var Q2;
            {var subQ1=sQuery(id+"F16.wireOp",EDGE,"E85");Q2=makeQuery(id+"F16.imprint","IMPRINT",FACE,{"disambiguationData":[TD([[makeQuery(id+"F16.imprint","IMPRINT",EDGE,{"derivedFrom":subQ1}),1.0]])]});}
            var Q3;
            Q3=makeQuery(id+"F16.imprint","IMPRINT",FACE,{"disambiguationData":[TD([[makeQuery(id+"F16.imprint","IMPRINT",EDGE,{"derivedFrom":makeQuery(id+"F1.opExtrude","CAP_EDGE",EDGE,{"disambiguationData":[OSD([sQuery(id+"F0.wireOp",EDGE,"E1.left")])],"isStart":true})}),-1.0]])]});
            extrude(context, id + "F17", {"entities" : qUnion([Q0, Q1, Q2, Q3]), "operationType" : NewBodyOperationType.ADD, "depth" : 5 * mm});
        }
    });
